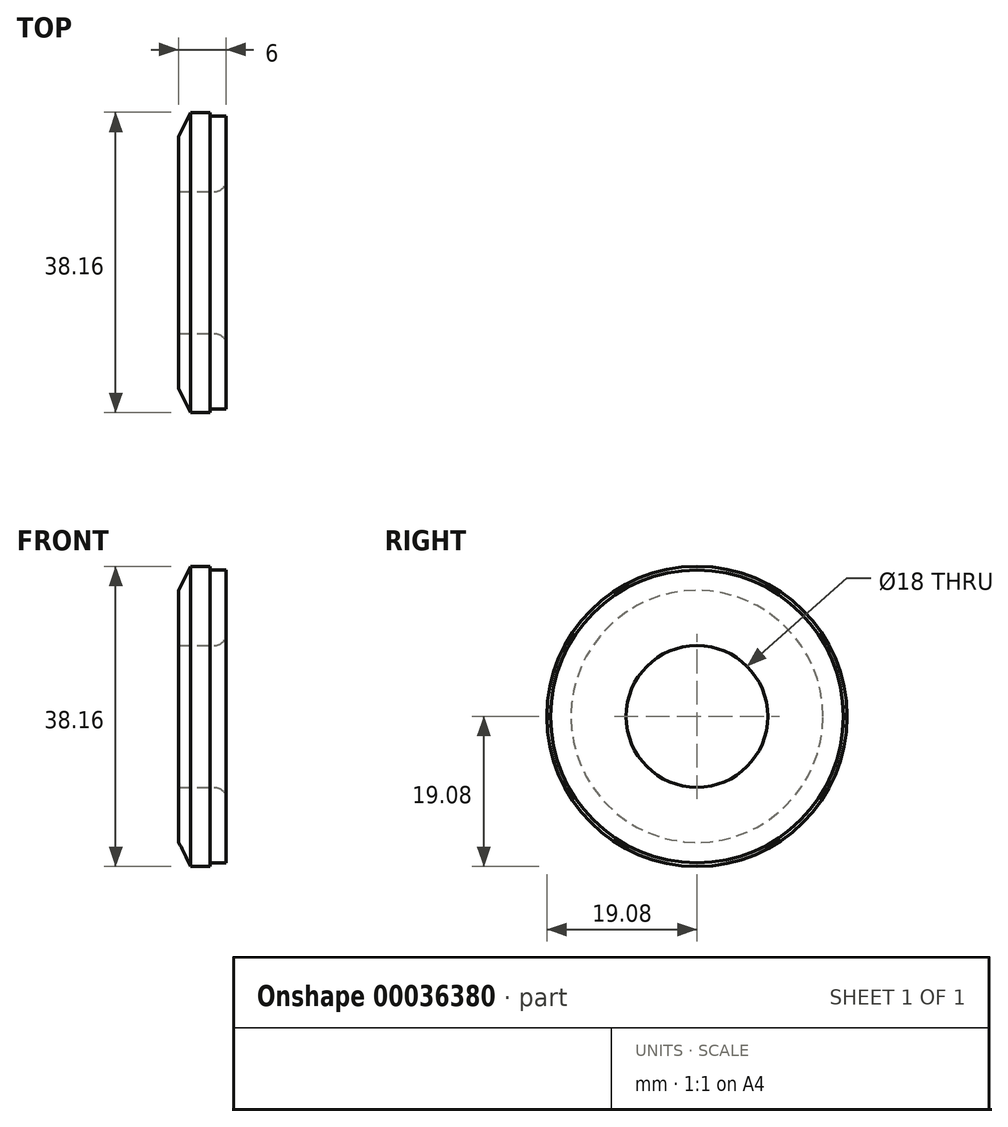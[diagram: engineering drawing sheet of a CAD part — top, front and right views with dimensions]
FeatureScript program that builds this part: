
annotation { "Feature Type Name" : "Feature", "Feature Type Description" : "" }
export const myFeature = defineFeature(function(context is Context, id is Id, definition is map)
    precondition{}
    {
        {
            var Q0;
            Q0=qCreatedBy(makeId("Front.planeOp"),FACE);
            var sketch = newSketch(context, id + "F0", { "sketchPlane" : qUnion([Q0])});
            skLineSegment(sketch, "E0", {"start": v(0, 9) * mm, "end": v(-6, 9) * mm});
            skLineSegment(sketch, "E1", {"start": v(-6, 9) * mm, "end": v(-6, 16) * mm});
            skLineSegment(sketch, "E2", {"start": v(-6, 16) * mm, "end": v(-4.5, 19.07) * mm});
            skLineSegment(sketch, "E3", {"start": v(-4.5, 19.07) * mm, "end": v(-2, 19.07) * mm});
            skLineSegment(sketch, "E4", {"start": v(-2, 19.07) * mm, "end": v(-2, 18.6) * mm});
            skLineSegment(sketch, "E5", {"start": v(-2, 18.6) * mm, "end": v(0, 18.6) * mm});
            skLineSegment(sketch, "E6", {"start": v(0, 18.6) * mm, "end": v(0, 9) * mm});
            skLineSegment(sketch, "E7", {"start": v(0, 0) * mm, "end": v(-21.11, 0) * mm, "construction": true});
            skSolve(sketch);
        }
        {
            var Q0;
            Q0=makeQuery(id+"F0.imprint","IMPRINT",FACE,{"disambiguationData":[TD([[makeQuery(id+"F0.imprint","IMPRINT",EDGE,{"derivedFrom":sQuery(id+"F0.wireOp",EDGE,"E0")}),-1.0]])]});
            var Q1;
            Q1=sQuery(id+"F0.wireOp",EDGE,"E7");
            revolve(context, id + "F1", {"entities" : qUnion([Q0]), "axis" : qUnion([Q1]), "revolveType" : RevolveType.FULL});
        }
        {
            var Q0;
            Q0=makeQuery(id+"F1.opRevolve","SWEPT_EDGE",EDGE,{"disambiguationData":[OSD([sQuery(id+"F0.wireOp",EDGE,"E0"),sQuery(id+"F0.wireOp",EDGE,"E6")])]});
            fillet(context, id + "F2", {"entities" : qUnion([Q0]), "radius" : 1.5 * mm, "tangentPropagation" : true, "allowEdgeOverflow" : false});
        }
    });
